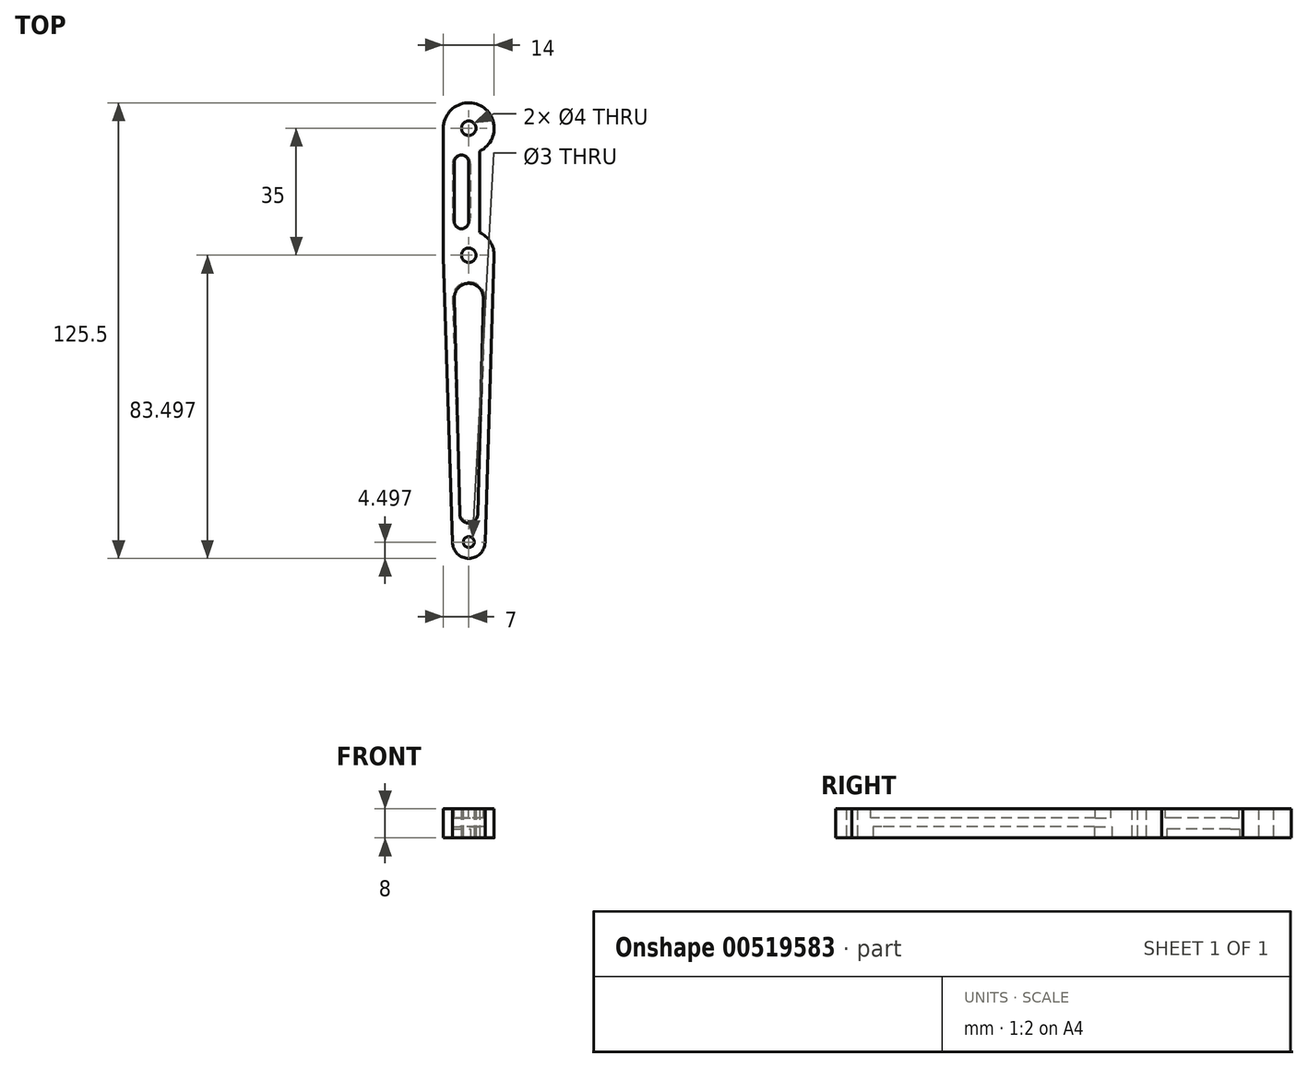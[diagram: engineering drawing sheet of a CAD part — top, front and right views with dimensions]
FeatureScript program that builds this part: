
annotation { "Feature Type Name" : "Feature", "Feature Type Description" : "" }
export const myFeature = defineFeature(function(context is Context, id is Id, definition is map)
    precondition{}
    {
        {
            var Q0;
            Q0=qCreatedBy(makeId("Top.planeOp"),FACE);
            var sketch = newSketch(context, id + "F0", { "sketchPlane" : qUnion([Q0])});
            skCircle(sketch, "E0", {"center": v(0, 49.25) * mm, "radius": 7 * mm});
            skCircle(sketch, "E1", {"center": v(0, 49.25) * mm, "radius": 2 * mm});
            skArc(sketch, "E2", {"start": v(7, 14.03) * mm, "mid": v(5.97, 17.9) * mm, "end": v(3, 20.57) * mm});
            skCircle(sketch, "E3", {"center": v(0, 14.25) * mm, "radius": 2 * mm});
            skLineSegment(sketch, "E4", {"start": v(3, 42.92) * mm, "end": v(3, 20.57) * mm});
            skLineSegment(sketch, "E5", {"start": v(-7, 49.25) * mm, "end": v(-7, 14.25) * mm});
            skArc(sketch, "E6", {"start": v(-4.5, -64.75) * mm, "mid": v(0, -69.25) * mm, "end": v(4.5, -64.75) * mm});
            skCircle(sketch, "E7", {"center": v(0, -64.75) * mm, "radius": 1.5 * mm});
            skLineSegment(sketch, "E8", {"start": v(-4.5, -64.75) * mm, "end": v(-7, 14.25) * mm});
            skLineSegment(sketch, "E9", {"start": v(4.5, -64.75) * mm, "end": v(7, 14.25) * mm});
            skArc(sketch, "E10.trimOffspring", {"start": v(-7, 14.25) * mm, "mid": v(-7, 14.03) * mm, "end": v(-6.99, 13.8) * mm});
            skSolve(sketch);
        }
        {
            var Q0;
            Q0 = qSketchRegion(id + "F0", true);
            extrude(context, id + "F1", {"entities" : qUnion([Q0]), "depth" : 8 * mm, "offsetDistance" : 25 * mm});
        }
        {
            var Q0;
            Q0=makeQuery(id+"F1.opExtrude","CAP_FACE",FACE,{"disambiguationData":[OSD([sQuery(id+"F0.wireOp",EDGE,"E0"),sQuery(id+"F0.wireOp",EDGE,"E1"),sQuery(id+"F0.wireOp",EDGE,"E2"),sQuery(id+"F0.wireOp",EDGE,"E3"),sQuery(id+"F0.wireOp",EDGE,"E4"),sQuery(id+"F0.wireOp",EDGE,"E5"),sQuery(id+"F0.wireOp",EDGE,"E6"),sQuery(id+"F0.wireOp",EDGE,"E7"),sQuery(id+"F0.wireOp",EDGE,"E8"),sQuery(id+"F0.wireOp",EDGE,"E9"),sQuery(id+"F0.wireOp",EDGE,"E10.trimOffspring")])],"isStart":false});
            var sketch = newSketch(context, id + "F2", { "sketchPlane" : qUnion([Q0])});
            skArc(sketch, "E11", {"start": v(4, 2.33) * mm, "mid": v(0, 6.53) * mm, "end": v(-4, 2.33) * mm});
            skArc(sketch, "E12", {"start": v(-2.5, -57.12) * mm, "mid": v(0, -59.55) * mm, "end": v(2.5, -57.12) * mm});
            skLineSegment(sketch, "E13", {"start": v(-4, 2.53) * mm, "end": v(-2.5, -57.12) * mm});
            skLineSegment(sketch, "E14", {"start": v(4, 2.53) * mm, "end": v(2.5, -57.12) * mm});
            skPoint(sketch, "E15.center.orphan", {"position": v(0, 14.25) * mm});
            skPoint(sketch, "E16.center.orphan", {"position": v(0, -64.75) * mm});
            skSolve(sketch);
        }
        {
            var Q0;
            Q0 = qSketchRegion(id + "F2", true);
            extrude(context, id + "F3", {"entities" : qUnion([Q0]), "operationType" : NewBodyOperationType.REMOVE, "oppositeDirection" : true, "depth" : 2.5 * mm, "offsetDistance" : 25 * mm});
        }
        {
            var Q0;
            Q0=makeQuery(id+"F1.opExtrude","CAP_FACE",FACE,{"disambiguationData":[OSD([sQuery(id+"F0.wireOp",EDGE,"E0"),sQuery(id+"F0.wireOp",EDGE,"E1"),sQuery(id+"F0.wireOp",EDGE,"E2"),sQuery(id+"F0.wireOp",EDGE,"E3"),sQuery(id+"F0.wireOp",EDGE,"E4"),sQuery(id+"F0.wireOp",EDGE,"E5"),sQuery(id+"F0.wireOp",EDGE,"E6"),sQuery(id+"F0.wireOp",EDGE,"E7"),sQuery(id+"F0.wireOp",EDGE,"E8"),sQuery(id+"F0.wireOp",EDGE,"E9"),sQuery(id+"F0.wireOp",EDGE,"E10.trimOffspring")])],"isStart":false});
            var sketch = newSketch(context, id + "F4", { "sketchPlane" : qUnion([Q0])});
            skArc(sketch, "E17", {"start": v(0, 39.86) * mm, "mid": v(-2, 41.86) * mm, "end": v(-4, 39.86) * mm});
            skArc(sketch, "E18", {"start": v(-4, 23.54) * mm, "mid": v(-2, 21.54) * mm, "end": v(0, 23.54) * mm});
            skLineSegment(sketch, "E19", {"start": v(-4, 39.86) * mm, "end": v(-4, 23.54) * mm});
            skLineSegment(sketch, "E20", {"start": v(0, 39.86) * mm, "end": v(0, 23.54) * mm});
            skPoint(sketch, "E21.orphan", {"position": v(-7, 31.75) * mm});
            skPoint(sketch, "E22.orphan", {"position": v(-2, 31.75) * mm});
            skPoint(sketch, "E23.trimOffspring.end.orphan", {"position": v(3, 31.75) * mm});
            skPoint(sketch, "E24.center.orphan", {"position": v(0, 49.25) * mm});
            skPoint(sketch, "E25.center.orphan", {"position": v(0, 14.25) * mm});
            skSolve(sketch);
        }
        {
            var Q0;
            Q0 = qSketchRegion(id + "F4", true);
            extrude(context, id + "F5", {"entities" : qUnion([Q0]), "operationType" : NewBodyOperationType.REMOVE, "oppositeDirection" : true, "depth" : 2.5 * mm, "offsetDistance" : 25 * mm});
        }
        {
            var Q0;
            Q0=makeQuery(id+"F1.opExtrude","CAP_FACE",FACE,{"disambiguationData":[OSD([sQuery(id+"F0.wireOp",EDGE,"E0"),sQuery(id+"F0.wireOp",EDGE,"E1"),sQuery(id+"F0.wireOp",EDGE,"E2"),sQuery(id+"F0.wireOp",EDGE,"E3"),sQuery(id+"F0.wireOp",EDGE,"E4"),sQuery(id+"F0.wireOp",EDGE,"E5"),sQuery(id+"F0.wireOp",EDGE,"E6"),sQuery(id+"F0.wireOp",EDGE,"E7"),sQuery(id+"F0.wireOp",EDGE,"E8"),sQuery(id+"F0.wireOp",EDGE,"E9"),sQuery(id+"F0.wireOp",EDGE,"E10.trimOffspring")])],"isStart":true});
            var sketch = newSketch(context, id + "F6", { "sketchPlane" : qUnion([Q0])});
            skArc(sketch, "E26", {"start": v(-4.5, -39.48) * mm, "mid": v(-2, -41.98) * mm, "end": v(0.5, -39.48) * mm});
            skArc(sketch, "E27", {"start": v(0.5, -24.48) * mm, "mid": v(-2, -21.98) * mm, "end": v(-4.5, -24.48) * mm});
            skLineSegment(sketch, "E28", {"start": v(0.5, -39.48) * mm, "end": v(0.5, -24.48) * mm});
            skLineSegment(sketch, "E29", {"start": v(-4.5, -39.48) * mm, "end": v(-4.5, -24.48) * mm});
            skPoint(sketch, "E30.orphan", {"position": v(-2, -31.75) * mm});
            skPoint(sketch, "E31.center.orphan", {"position": v(0, -49.25) * mm});
            skPoint(sketch, "E32.center.orphan", {"position": v(0, -14.25) * mm});
            skSolve(sketch);
        }
        {
            var Q0;
            Q0 = qSketchRegion(id + "F6", true);
            extrude(context, id + "F7", {"entities" : qUnion([Q0]), "operationType" : NewBodyOperationType.REMOVE, "oppositeDirection" : true, "depth" : 2.5 * mm, "offsetDistance" : 25 * mm});
        }
        {
            var Q0;
            Q0=makeQuery(id+"F1.opExtrude","CAP_FACE",FACE,{"disambiguationData":[OSD([sQuery(id+"F0.wireOp",EDGE,"E0"),sQuery(id+"F0.wireOp",EDGE,"E1"),sQuery(id+"F0.wireOp",EDGE,"E2"),sQuery(id+"F0.wireOp",EDGE,"E3"),sQuery(id+"F0.wireOp",EDGE,"E4"),sQuery(id+"F0.wireOp",EDGE,"E5"),sQuery(id+"F0.wireOp",EDGE,"E6"),sQuery(id+"F0.wireOp",EDGE,"E7"),sQuery(id+"F0.wireOp",EDGE,"E8"),sQuery(id+"F0.wireOp",EDGE,"E9"),sQuery(id+"F0.wireOp",EDGE,"E10.trimOffspring")])],"isStart":true});
            var sketch = newSketch(context, id + "F8", { "sketchPlane" : qUnion([Q0])});
            skArc(sketch, "E33", {"start": v(-4.49, -2.08) * mm, "mid": v(0, -6.88) * mm, "end": v(4.49, -2.08) * mm});
            skArc(sketch, "E34", {"start": v(2.5, 56.55) * mm, "mid": v(0, 58.96) * mm, "end": v(-2.5, 56.55) * mm});
            skLineSegment(sketch, "E35", {"start": v(4.5, -2.38) * mm, "end": v(2.5, 56.55) * mm});
            skLineSegment(sketch, "E36", {"start": v(-4.5, -2.38) * mm, "end": v(-2.5, 56.55) * mm});
            skPoint(sketch, "E37.center.orphan", {"position": v(0, 64.75) * mm});
            skSolve(sketch);
        }
        {
            var Q0;
            Q0 = qSketchRegion(id + "F8", true);
            extrude(context, id + "F9", {"entities" : qUnion([Q0]), "operationType" : NewBodyOperationType.REMOVE, "oppositeDirection" : true, "depth" : 3.1 * mm, "offsetDistance" : 25 * mm});
        }
    });
